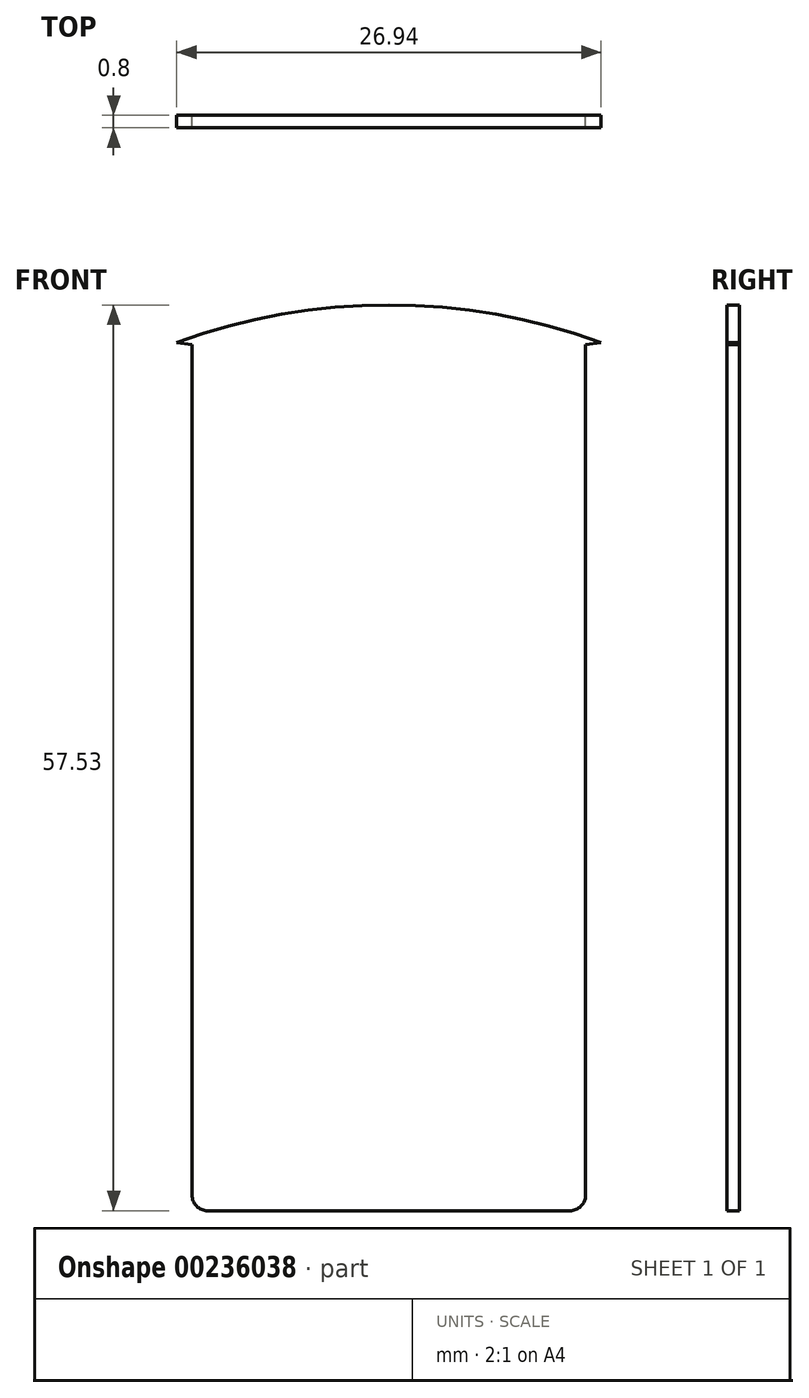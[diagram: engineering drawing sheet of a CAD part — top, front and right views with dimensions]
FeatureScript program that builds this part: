
annotation { "Feature Type Name" : "Feature", "Feature Type Description" : "" }
export const myFeature = defineFeature(function(context is Context, id is Id, definition is map)
    precondition{}
    {
        {
            var Q0;
            Q0=qCreatedBy(makeId("Front.planeOp"),FACE);
            var sketch = newSketch(context, id + "F0", { "sketchPlane" : qUnion([Q0])});
            skLineSegment(sketch, "E0.bottom", {"start": v(0, 36.65) * mm, "end": v(-12.5, 36.65) * mm});
            skLineSegment(sketch, "E0.top", {"start": v(0, -18.35) * mm, "end": v(-11.5, -18.35) * mm});
            skLineSegment(sketch, "E0.left", {"start": v(0, 36.65) * mm, "end": v(0, -18.35) * mm});
            skLineSegment(sketch, "E0.right", {"start": v(-12.5, 36.65) * mm, "end": v(-12.5, -17.35) * mm});
            skLineSegment(sketch, "E1.MirrorCS", {"start": v(0, 36.65) * mm, "end": v(12.5, 36.65) * mm});
            skLineSegment(sketch, "E2.MirrorCS", {"start": v(12.5, 36.65) * mm, "end": v(12.5, -17.35) * mm});
            skLineSegment(sketch, "E3.MirrorCS", {"start": v(0, -18.35) * mm, "end": v(11.5, -18.35) * mm});
            skLineSegment(sketch, "E4", {"start": v(-12.5, 36.65) * mm, "end": v(-13.47, 36.79) * mm});
            skArc(sketch, "E5", {"start": v(-13.47, 36.79) * mm, "mid": v(-6.84, 38.58) * mm, "end": v(0, 39.18) * mm});
            skArc(sketch, "E6.MirrorCS", {"start": v(13.47, 36.79) * mm, "mid": v(6.84, 38.58) * mm, "end": v(0, 39.18) * mm});
            skLineSegment(sketch, "E7.MirrorCS", {"start": v(12.5, 36.65) * mm, "end": v(13.47, 36.79) * mm});
            skPoint(sketch, "E8.visualSharp", {"position": v(-12.5, -18.35) * mm});
            skArc(sketch, "E8.filletArc", {"start": v(-12.5, -17.35) * mm, "mid": v(-12.2, -18.06) * mm, "end": v(-11.5, -18.35) * mm});
            skPoint(sketch, "E9.visualSharp", {"position": v(12.5, -18.35) * mm});
            skArc(sketch, "E9.filletArc", {"start": v(11.5, -18.35) * mm, "mid": v(12.2, -18.06) * mm, "end": v(12.5, -17.35) * mm});
            skSolve(sketch);
        }
        {
            var Q0;
            Q0=makeQuery(id+"F0.imprint","IMPRINT",FACE,{"disambiguationData":[TD([[makeQuery(id+"F0.imprint","IMPRINT",EDGE,{"derivedFrom":sQuery(id+"F0.wireOp",EDGE,"E0.bottom")}),1.0]])]});
            var Q1;
            Q1=makeQuery(id+"F0.imprint","IMPRINT",FACE,{"disambiguationData":[TD([[makeQuery(id+"F0.imprint","IMPRINT",EDGE,{"derivedFrom":sQuery(id+"F0.wireOp",EDGE,"E0.bottom")}),-1.0]])]});
            var Q2;
            Q2=makeQuery(id+"F0.imprint","IMPRINT",FACE,{"disambiguationData":[TD([[makeQuery(id+"F0.imprint","IMPRINT",EDGE,{"derivedFrom":sQuery(id+"F0.wireOp",EDGE,"E0.left")}),1.0]])]});
            extrude(context, id + "F1", {"entities" : qUnion([Q0, Q1, Q2]), "depth" : 0.8 * mm});
        }
    });
